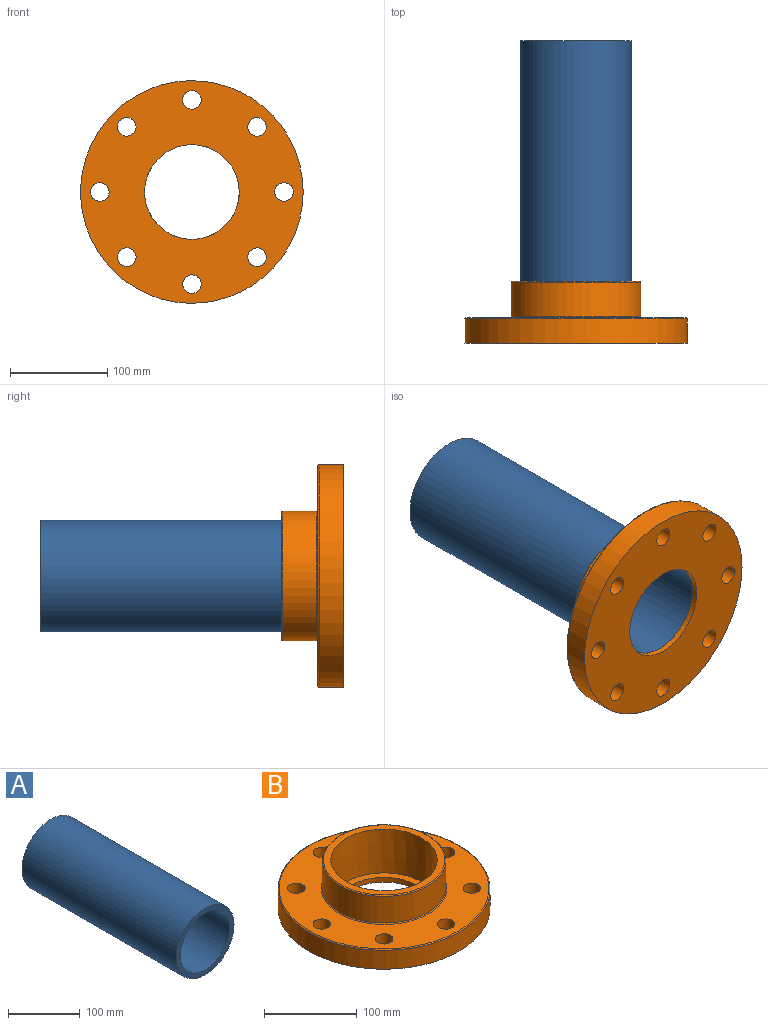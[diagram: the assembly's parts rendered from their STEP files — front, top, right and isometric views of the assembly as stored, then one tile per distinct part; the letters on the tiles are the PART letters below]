
ASSEMBLY  parts=2 mates=1
PART A: 4 faces, bbox 114.3x304.8x114.3 mm
  f0: cylinder r=48.59mm len=304.8mm, axis (0,1,0), area 93055.8mm2, adj f2,f3
  f1: cylinder r=57.15mm len=304.8mm, axis (0,1,0), area 109448.8mm2, adj f2,f3
  f2: plane 114.3x114.3mm, normal (0,-1,0), area 2843.5mm2, adj f0,f1
  f3: plane 114.3x114.3mm, normal (0,1,0), area 2843.5mm2, adj f0,f1
PART B: 19 faces, bbox 247.4x247.4x63.5 mm
  f0: cylinder r=48.59mm len=97.18mm, axis (0,0,-1), area 1861.1mm2, adj f16,f18
  f1: cone r=57.04mm half-angle=0.3deg, axis (0,0,1), area 20633.8mm2, adj f17,f18
  f2: torus R=113.15mm, axis (0,0,1), area 1297.7mm2, adj f14,f15
  f3: torus R=67.7mm, axis (0,0,1), area 763.1mm2, adj f13,f15
  f4: torus R=65.39mm, axis (0,0,1), area 753.5mm2, adj f13,f17
  f5: cylinder r=9.53mm len=26.16mm, axis (0,0,1), area 1565.7mm2, adj f15,f16
  f6: cylinder r=9.53mm len=26.16mm, axis (0,0,1), area 1565.7mm2, adj f15,f16
  f7: cylinder r=9.53mm len=26.16mm, axis (0,0,1), area 1565.7mm2, adj f15,f16
  f8: cylinder r=9.53mm len=26.16mm, axis (0,0,1), area 1565.7mm2, adj f15,f16
  f9: cylinder r=9.53mm len=26.16mm, axis (0,0,1), area 1565.7mm2, adj f15,f16
  f10: cylinder r=9.53mm len=26.16mm, axis (0,0,1), area 1565.7mm2, adj f15,f16
  f11: cylinder r=9.53mm len=26.16mm, axis (0,0,1), area 1565.7mm2, adj f15,f16
  f12: cylinder r=9.53mm len=26.16mm, axis (0,0,1), area 1565.7mm2, adj f15,f16
  f13: cylinder r=66.55mm len=133.1mm, axis (0,0,-1), area 14646.8mm2, adj f3,f4
  f14: cylinder r=114.3mm len=228.6mm, axis (0,0,-1), area 17959.6mm2, adj f2,f16
  f15: plane 226.29x226.29mm, normal (0,0,1), area 23538.2mm2, adj f2,f3,f5,f6,f7,f8,f9,f10
  f16: plane 228.6x228.6mm, normal (0,0,-1), area 31345.8mm2, adj f0,f5,f6,f7,f8,f9,f10,f11
  f17: plane 130.79x130.79mm, normal (0,0,1), area 3091.3mm2, adj f1,f4
  f18: plane 114.07x114.07mm, normal (0,0,1), area 2802.5mm2, adj f0,f1
PLACE A t=(-170.98,-51.06,71.48)mm fixed
PLACE B rot(axis=(-1,0,0),90deg) t=(-170.98,-209.56,71.48)mm
MATE fastened B.f1 <-> A.f0  axis (0,1,0) through (-170.98,-203.46,71.48)mm
